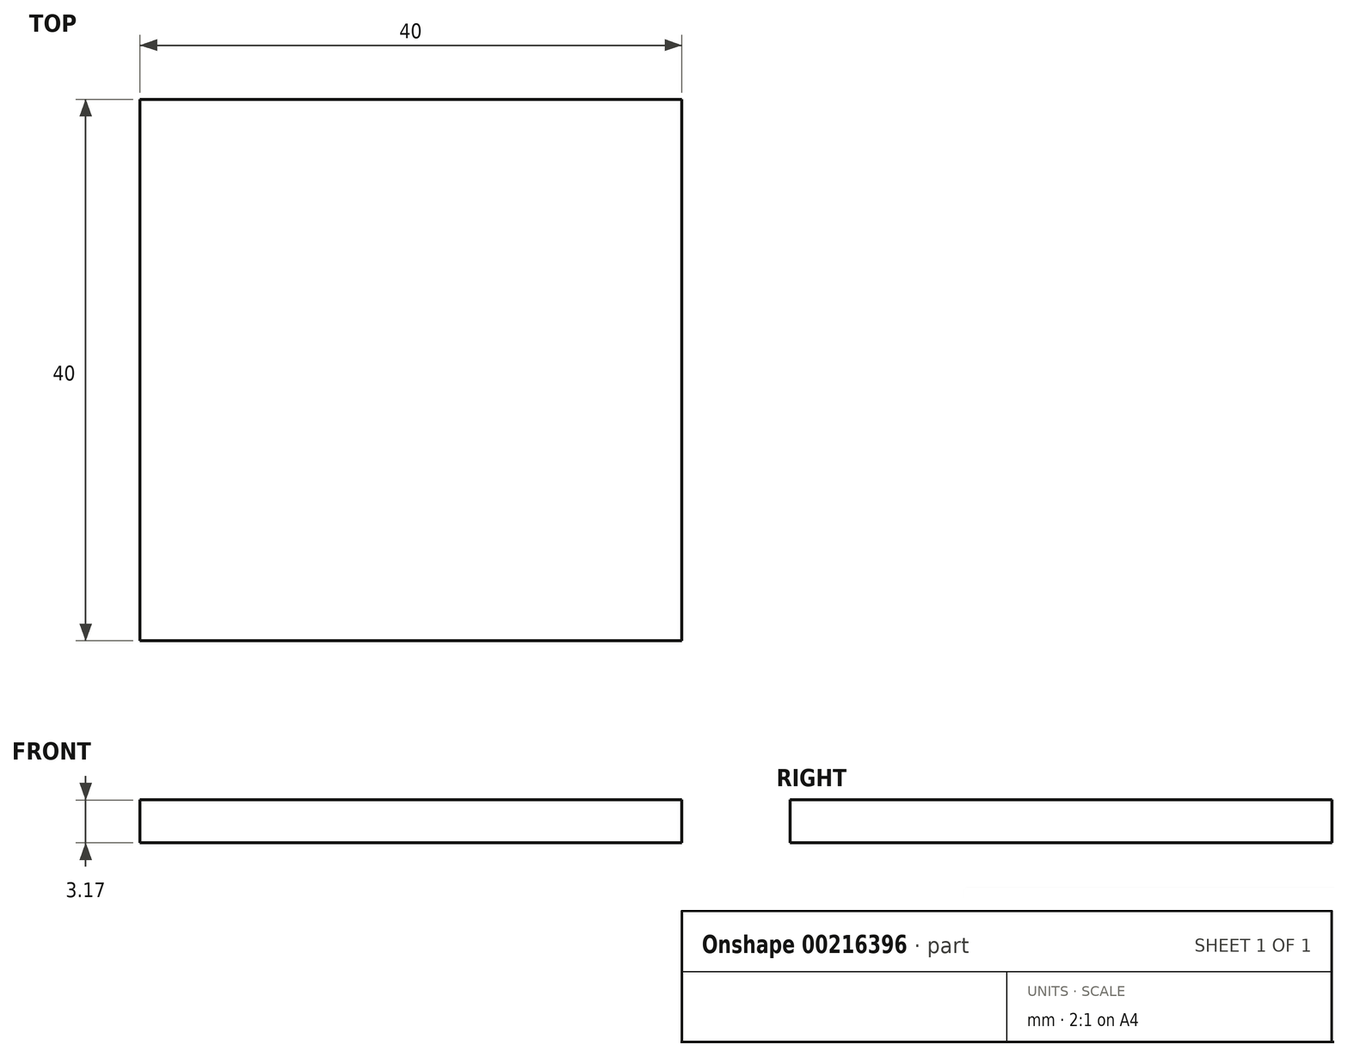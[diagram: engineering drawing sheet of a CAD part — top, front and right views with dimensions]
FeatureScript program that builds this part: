
annotation { "Feature Type Name" : "Feature", "Feature Type Description" : "" }
export const myFeature = defineFeature(function(context is Context, id is Id, definition is map)
    precondition{}
    {
        {
            var Q0;
            Q0=qCreatedBy(makeId("Top.planeOp"),FACE);
            var sketch = newSketch(context, id + "F0", { "sketchPlane" : qUnion([Q0])});
            skLineSegment(sketch, "E0.bottom", {"start": v(-3.7, 0) * mm, "end": v(-43.7, 0) * mm});
            skLineSegment(sketch, "E0.top", {"start": v(-3.7, -40) * mm, "end": v(-43.7, -40) * mm});
            skLineSegment(sketch, "E0.left", {"start": v(-3.7, 0) * mm, "end": v(-3.7, -40) * mm});
            skLineSegment(sketch, "E0.right", {"start": v(-43.7, 0) * mm, "end": v(-43.7, -40) * mm});
            skSolve(sketch);
        }
        {
            var Q0;
            Q0 = qSketchRegion(id + "F0", true);
            extrude(context, id + "F1", {"entities" : qUnion([Q0]), "depth" : 3.17 * mm});
        }
    });
